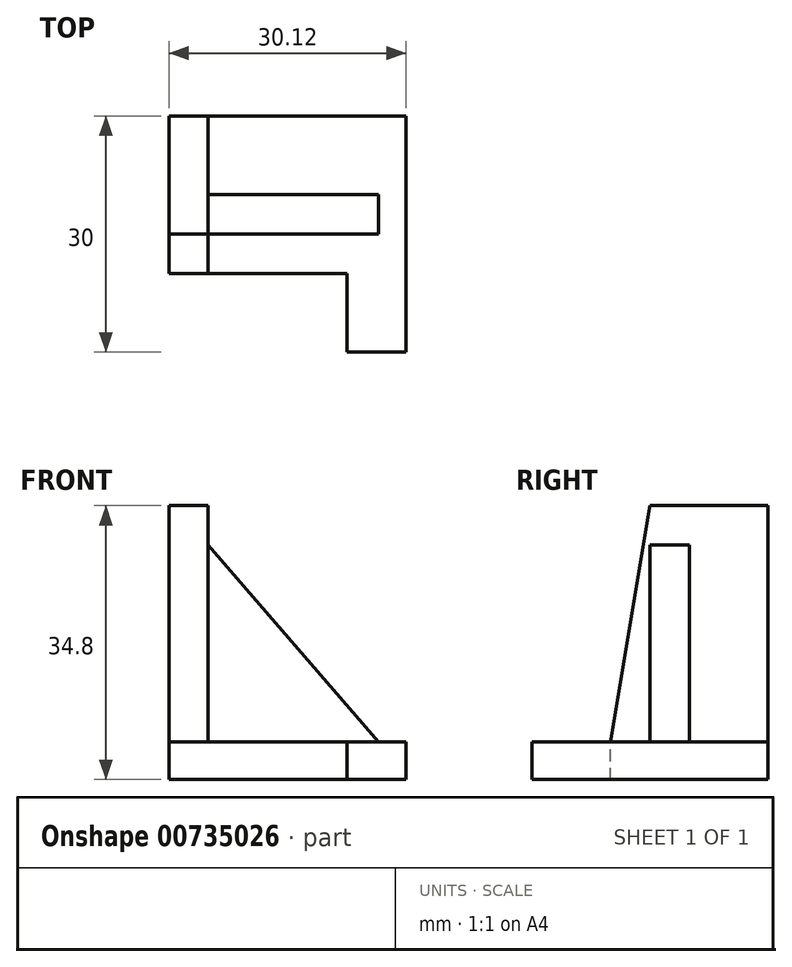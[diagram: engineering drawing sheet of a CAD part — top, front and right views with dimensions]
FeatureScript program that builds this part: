
annotation { "Feature Type Name" : "Feature", "Feature Type Description" : "" }
export const myFeature = defineFeature(function(context is Context, id is Id, definition is map)
    precondition{}
    {
        {
            var Q0;
            Q0=qCreatedBy(makeId("Front.planeOp"),FACE);
            var sketch = newSketch(context, id + "F0", { "sketchPlane" : qUnion([Q0])});
            skLineSegment(sketch, "E0", {"start": v(0, 25) * mm, "end": v(0, 0) * mm});
            skLineSegment(sketch, "E1", {"start": v(0, 0) * mm, "end": v(21.64, 0) * mm});
            skLineSegment(sketch, "E2", {"start": v(21.64, 0) * mm, "end": v(0, 25) * mm});
            skSolve(sketch);
        }
        {
            var Q0;
            Q0=makeQuery(id+"F0.imprint","IMPRINT",FACE,{"disambiguationData":[TD([[makeQuery(id+"F0.imprint","IMPRINT",EDGE,{"derivedFrom":sQuery(id+"F0.wireOp",EDGE,"E0")}),1.0]])]});
            extrude(context, id + "F1", {"entities" : qUnion([Q0]), "depth" : 5 * mm, "offsetDistance" : 25.4 * mm});
        }
        {
            var Q0;
            Q0=qCreatedBy(makeId("Right.planeOp"),FACE);
            var sketch = newSketch(context, id + "F2", { "sketchPlane" : qUnion([Q0])});
            skLineSegment(sketch, "E3", {"start": v(10, 0) * mm, "end": v(10, 30) * mm});
            skLineSegment(sketch, "E4", {"start": v(10, 30) * mm, "end": v(-5, 30) * mm});
            skLineSegment(sketch, "E5", {"start": v(-5, 30) * mm, "end": v(-10, 0) * mm});
            skLineSegment(sketch, "E6", {"start": v(-10, 0) * mm, "end": v(10, 0) * mm});
            skSolve(sketch);
        }
        {
            var Q0;
            Q0 = qSketchRegion(id + "F2", true);
            extrude(context, id + "F3", {"entities" : qUnion([Q0]), "operationType" : NewBodyOperationType.ADD, "oppositeDirection" : true, "depth" : 5 * mm, "offsetDistance" : 25 * mm});
        }
        {
            var Q0;
            Q0=qCreatedBy(makeId("Top.planeOp"),FACE);
            var sketch = newSketch(context, id + "F4", { "sketchPlane" : qUnion([Q0])});
            skLineSegment(sketch, "E7.bottom", {"start": v(-5, -10) * mm, "end": v(25.12, -10) * mm});
            skLineSegment(sketch, "E7.top", {"start": v(-5, 10) * mm, "end": v(25.12, 10) * mm});
            skLineSegment(sketch, "E7.left", {"start": v(-5, -10) * mm, "end": v(-5, 10) * mm});
            skLineSegment(sketch, "E7.right", {"start": v(25.12, -10) * mm, "end": v(25.12, 10) * mm});
            skLineSegment(sketch, "E8.top", {"start": v(25.12, -20) * mm, "end": v(17.62, -20) * mm});
            skLineSegment(sketch, "E8.left", {"start": v(25.12, -10) * mm, "end": v(25.12, -20) * mm});
            skLineSegment(sketch, "E8.right", {"start": v(17.62, -10) * mm, "end": v(17.62, -20) * mm});
            skSolve(sketch);
        }
        {
            var Q0;
            Q0 = qSketchRegion(id + "F4", true);
            var Q1;
            Q1=makeQuery(id+"F4.imprint","IMPRINT",FACE,{"disambiguationData":[TD([[makeQuery(id+"F4.imprint","IMPRINT",EDGE,{"derivedFrom":sQuery(id+"F4.wireOp",EDGE,"E7.top")}),-1.0]])]});
            extrude(context, id + "F5", {"entities" : qUnion([Q0, Q1]), "operationType" : NewBodyOperationType.ADD, "oppositeDirection" : true, "depth" : 4.8 * mm, "offsetDistance" : 25 * mm});
        }
    });
